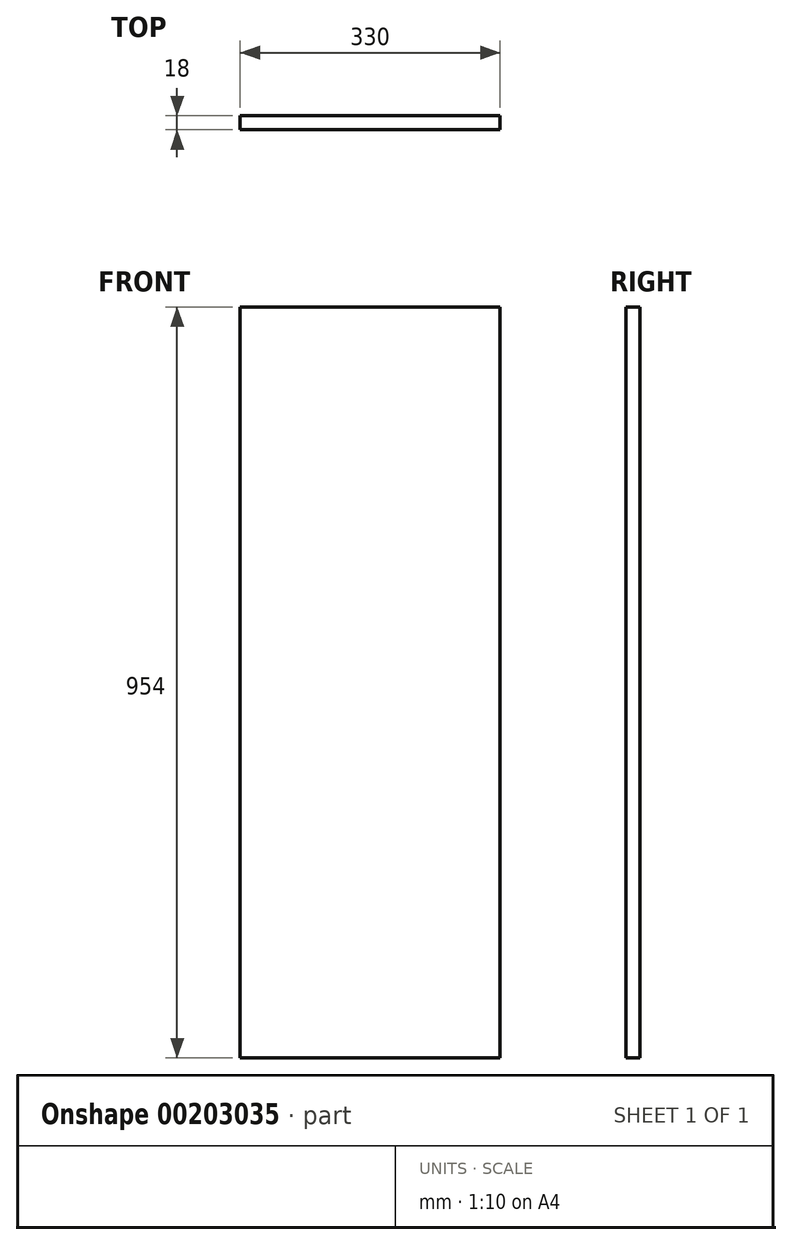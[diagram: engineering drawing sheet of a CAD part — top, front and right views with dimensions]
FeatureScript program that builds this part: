
annotation { "Feature Type Name" : "Feature", "Feature Type Description" : "" }
export const myFeature = defineFeature(function(context is Context, id is Id, definition is map)
    precondition{}
    {
        {
            var Q0;
            Q0=qCreatedBy(makeId("Front.planeOp"),FACE);
            var sketch = newSketch(context, id + "F0", { "sketchPlane" : qUnion([Q0])});
            skLineSegment(sketch, "E0.bottom", {"start": v(-165, -477) * mm, "end": v(165, -477) * mm});
            skLineSegment(sketch, "E0.top", {"start": v(-165, 477) * mm, "end": v(165, 477) * mm});
            skLineSegment(sketch, "E0.left", {"start": v(-165, -477) * mm, "end": v(-165, 477) * mm});
            skLineSegment(sketch, "E0.right", {"start": v(165, -477) * mm, "end": v(165, 477) * mm});
            skPoint(sketch, "E0.middle", {"position": v(0, 0) * mm});
            skSolve(sketch);
        }
        {
            var Q0;
            Q0=makeQuery(id+"F0.imprint","IMPRINT",FACE,{"disambiguationData":[TD([[makeQuery(id+"F0.imprint","IMPRINT",EDGE,{"derivedFrom":sQuery(id+"F0.wireOp",EDGE,"E0.bottom")}),1.0]])]});
            extrude(context, id + "F1", {"entities" : qUnion([Q0]), "depth" : 18 * mm});
        }
    });
